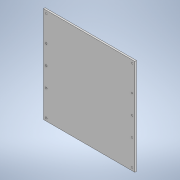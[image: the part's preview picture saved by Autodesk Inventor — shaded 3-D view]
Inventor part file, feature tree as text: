
AUTODESK INVENTOR PART (.ipt)
format: ipt  version: 2021 (Build 250183000, 183)  size: 159,232 bytes
history: native  units: mm
features: sketch x4, extrude x3, projected_geometry x2, pattern_linear x1, hole x1
ambient origin geometry x8: Origin, YZ Plane, XZ Plane, XY Plane, X Axis, Y Axis, Z Axis, Center Point
bodies: Solid1 (feature_tree)
feature tree (11):
  extrude  "Extrusion1"  Depth=4.0mm
  pattern_linear  "Rectangular Pattern1"  Count1=11  [1 undecoded]
  extrude  "Extrusion2"  Depth=82.0mm
  extrude  "Extrusion3"  Depth=3.5mm
  hole  "Hole1"  [1 undecoded]
  sketch  "Sketch1"  dims[d0=1.0mm d1=4.0mm d2=110.0mm]
  sketch  "Sketch2"  dims[d3=40.4mm d5=82.0mm]
  sketch  "Sketch3"  dims[d6=3.5mm d7=0.0mm d8=40.0mm d10=40.4mm]
  sketch  "Sketch4"  dims[d11=20.0mm d12=0.0mm d13=20.0mm d14=0.0mm d15=6.0mm d16=6.0mm d17=6.0mm d18=6.0mm d19=6.0mm d20=6.0mm d21=3.4mm d22=6.0mm d23=6.3mm d24=2.0mm d25=90.0deg d26=8.0mm d27=20.594885mm]
  projected_geometry  "Project Cut Edges1"
  projected_geometry  "Project Cut Edges2"
note: 2 required parameter values undecoded (feature->parameter linkage not recoverable at this tier; creation-order binding heuristic only, values carry confidence <= 0.55)
